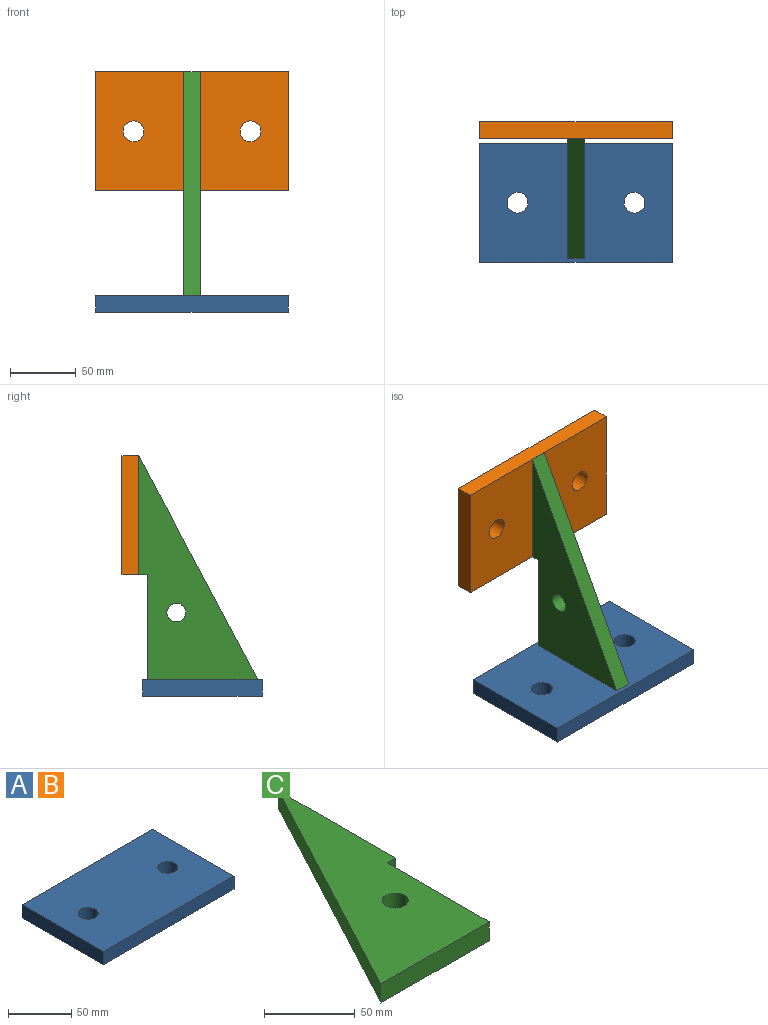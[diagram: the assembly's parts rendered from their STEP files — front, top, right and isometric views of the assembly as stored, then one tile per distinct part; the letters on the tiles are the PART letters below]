
ASSEMBLY  parts=3 mates=3
PART A: 8 faces, bbox 146.1x90.5x12.7 mm
  f0: plane 90.49x12.7mm, normal (-1,0,0), area 1149.2mm2, adj f1,f4,f6,f7
  f1: plane 146.05x12.7mm, normal (0,-1,0), area 1854.8mm2, adj f0,f2,f6,f7
  f2: plane 90.49x12.7mm, normal (1,0,0), area 1149.2mm2, adj f1,f4,f6,f7
  f3: cylinder r=7.94mm len=15.88mm, axis (0,0,-1), area 633.4mm2, adj f6,f7
  f4: plane 146.05x12.7mm, normal (0,1,0), area 1854.8mm2, adj f0,f2,f6,f7
  f5: cylinder r=7.94mm len=15.88mm, axis (0,0,-1), area 633.4mm2, adj f6,f7
  f6: plane 146.05x90.49mm, normal (0,0,1), area 12819.8mm2, adj f0,f1,f2,f3,f4,f5
  f7: plane 146.05x90.49mm, normal (0,0,-1), area 12819.8mm2, adj f0,f1,f2,f3,f4,f5
PART B: same geometry as A
PART C: 8 faces, bbox 90.5x169.9x12.7 mm
  f0: plane 90.49x12.7mm, normal (1,0,0), area 1149.2mm2, adj f1,f5,f6,f7
  f1: plane 169.86x90.49mm, normal (-0.88,0.47,0), area 2444.3mm2, adj f0,f2,f6,f7
  f2: plane 84.14x12.7mm, normal (0,-1,0), area 1068.5mm2, adj f1,f3,f6,f7
  f3: plane 79.38x12.7mm, normal (1,0,0), area 1008.1mm2, adj f2,f5,f6,f7
  f4: cylinder r=7.14mm len=14.29mm, axis (0,0,-1), area 570mm2, adj f6,f7
  f5: plane 12.7x6.35mm, normal (0,-1,0), area 80.6mm2, adj f0,f3,f6,f7
  f6: plane 169.86x90.49mm, normal (0,0,1), area 7020.9mm2, adj f0,f1,f2,f3,f4,f5
  f7: plane 169.86x90.49mm, normal (0,0,-1), area 7020.9mm2, adj f0,f1,f2,f3,f4,f5
PLACE A t=(-29.87,-25.57,-96.45)mm
PLACE B rot(axis=(1,0,0),90deg) t=(-29.87,29.2,34.52)mm
PLACE C rot(axis=(0.58,0.58,0.58),120deg) t=(-29.87,-5.72,-39.3)mm
MATE planar B.f1 <-> C.f5  axis (0,0,-1) through (-29.87,29.2,-10.73)mm
MATE fastened B.f6 <-> C.f0  axis (0,-1,0) through (-29.87,22.85,34.52)mm
MATE fastened C.f2 <-> A.f6  axis (0,0,-1) through (-29.87,-25.57,-90.1)mm
